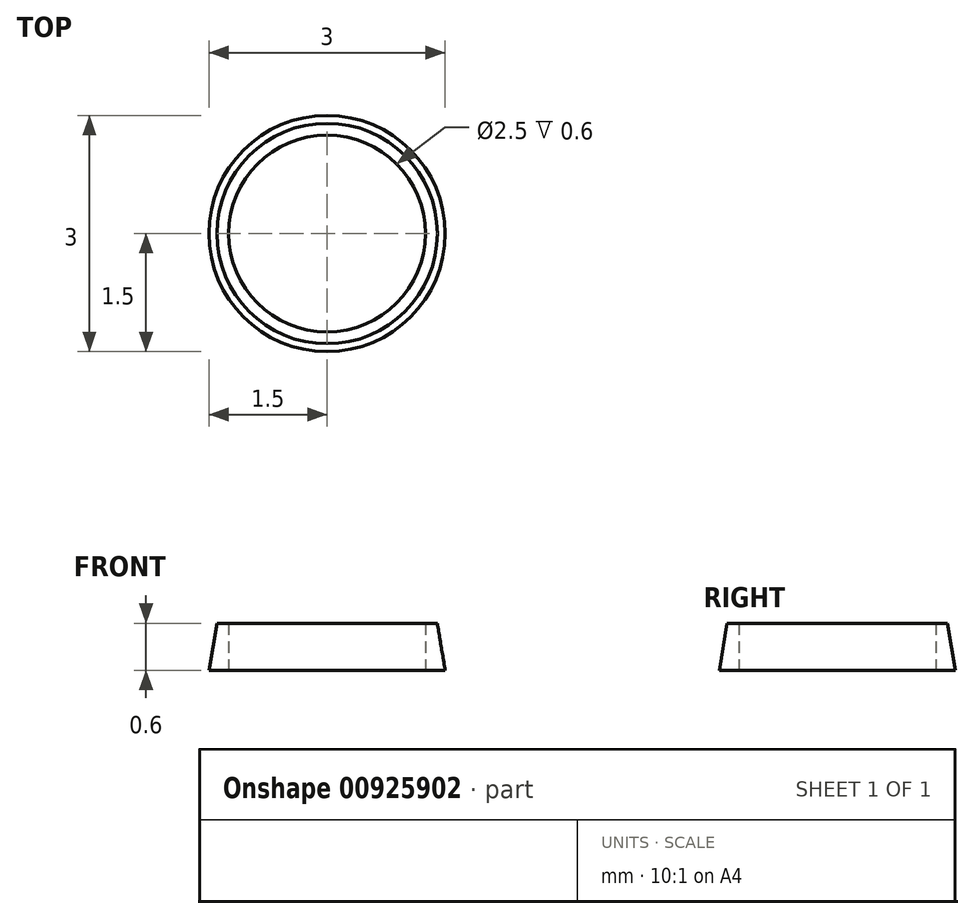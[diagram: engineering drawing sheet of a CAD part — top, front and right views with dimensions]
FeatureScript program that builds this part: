
annotation { "Feature Type Name" : "Feature", "Feature Type Description" : "" }
export const myFeature = defineFeature(function(context is Context, id is Id, definition is map)
    precondition{}
    {
        {
            var Q0;
            Q0=qCreatedBy(makeId("Top.planeOp"),FACE);
            var sketch = newSketch(context, id + "F0", { "sketchPlane" : qUnion([Q0])});
            skCircle(sketch, "E0", {"center": v(0, 0) * mm, "radius": 1.5 * mm});
            skSolve(sketch);
        }
        {
            var Q0;
            Q0 = qSketchRegion(id + "F0", true);
            extrude(context, id + "F1", {"entities" : qUnion([Q0]), "depth" : 0.6 * mm, "offsetDistance" : 25 * mm});
        }
        {
            var Q0;
            Q0=sQuery(id+"F0.wireOp",VERTEX,"E0.center");
            var Q1;
            Q1=makeQuery(id+"F1.opExtrude","SWEPT_BODY",BODY,{"disambiguationData":[OSD([sQuery(id+"F0.wireOp",EDGE,"E0")])]});
            hole(context, id + "F2", {"style" : HoleStyle.SIMPLE, "endStyle" : HoleEndStyle.THROUGH, "oppositeDirection" : true, "standardTappedOrClearance" : lookupTablePath({ "standard" : "ISO", "engagement" : "75%", "pitch" : "0.5 mm", "size" : "M3", "type" : "Tapped" }), "standardBlindInLast" : lookupTablePath({ "standard" : "ISO", "fit" : "Normal", "engagement" : "75%", "pitch" : "0.5 mm", "size" : "M3", "type" : "Clearance & tapped" }), "holeDiameter" : 2.5 * mm, "majorDiameter" : 3 * mm, "showTappedDepth" : true, "isTappedThrough" : true, "tappedDepth" : 1.2 * mm, "tapClearance" : 3, "startFromSketch" : true, "locations" : qUnion([Q0]), "scope" : qUnion([Q1])});
        }
        {
            var Q0;
            Q0=makeQuery(id+"F1.opExtrude","CAP_EDGE",EDGE,{"disambiguationData":[OSD([sQuery(id+"F0.wireOp",EDGE,"E0")])],"isStart":false});
            chamfer(context, id + "F3", {"entities" : qUnion([Q0]), "chamferType" : ChamferType.TWO_OFFSETS, "width1" : 0.1 * mm, "oppositeDirection" : false, "width2" : 0.6 * mm, "tangentPropagation" : true});
        }
    });
